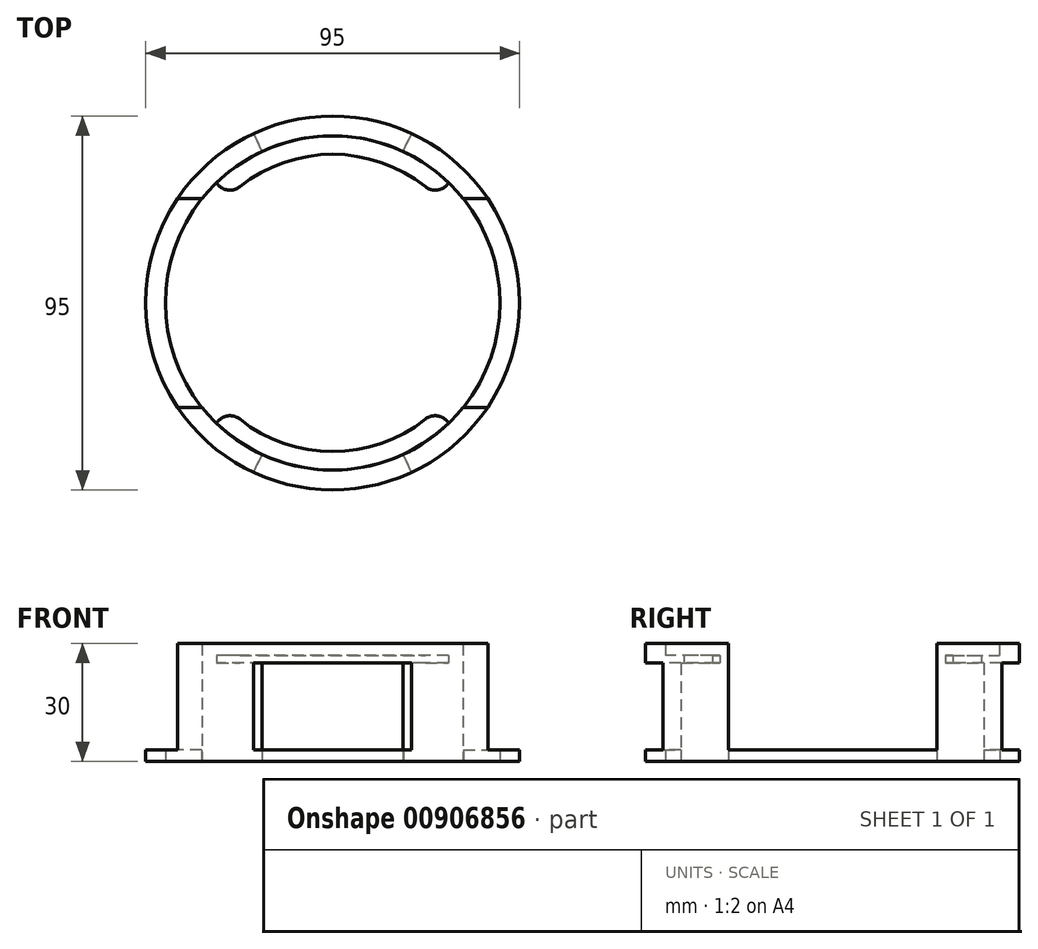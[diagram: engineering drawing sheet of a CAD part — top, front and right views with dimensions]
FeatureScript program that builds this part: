
annotation { "Feature Type Name" : "Feature", "Feature Type Description" : "" }
export const myFeature = defineFeature(function(context is Context, id is Id, definition is map)
    precondition{}
    {
        {
            var Q0;
            Q0=qCreatedBy(makeId("Top.planeOp"),FACE);
            var sketch = newSketch(context, id + "F0", { "sketchPlane" : qUnion([Q0])});
            skCircle(sketch, "E0", {"center": v(0, 0) * mm, "radius": 47.5 * mm});
            skCircle(sketch, "E1", {"center": v(0, 0) * mm, "radius": 42.5 * mm});
            skSolve(sketch);
        }
        {
            var Q0;
            Q0 = qSketchRegion(id + "F0", true);
            extrude(context, id + "F1", {"entities" : qUnion([Q0]), "depth" : 3 * mm, "offsetDistance" : 25 * mm});
        }
        {
            var Q0;
            Q0=qCreatedBy(makeId("Top.planeOp"),FACE);
            var sketch = newSketch(context, id + "F2", { "sketchPlane" : qUnion([Q0])});
            skLineSegment(sketch, "E2", {"start": v(0, 0) * mm, "end": v(-30.48, 65.37) * mm, "construction": true});
            skArc(sketch, "E3", {"start": v(-20.07, 43.05) * mm, "mid": v(-30.88, 36.1) * mm, "end": v(-39.42, 26.5) * mm});
            skLineSegment(sketch, "E4", {"start": v(-20.07, 43.05) * mm, "end": v(-17.94, 38.48) * mm});
            skLineSegment(sketch, "E5", {"start": v(-59.94, 25.5) * mm, "end": v(67.22, 25.5) * mm, "construction": true});
            skLineSegment(sketch, "E6.MirrorCS", {"start": v(-59.94, -25.5) * mm, "end": v(67.22, -25.5) * mm, "construction": true});
            skArc(sketch, "E7", {"start": v(-17.94, 38.48) * mm, "mid": v(-26.25, 33.37) * mm, "end": v(-33.17, 26.5) * mm});
            skLineSegment(sketch, "E8", {"start": v(-39.42, 26.5) * mm, "end": v(-33.17, 26.5) * mm});
            skLineSegment(sketch, "E9", {"start": v(-17.94, 38.48) * mm, "end": v(-20.07, 43.05) * mm});
            skLineSegment(sketch, "E10.MirrorCS", {"start": v(-17.94, -38.48) * mm, "end": v(-20.07, -43.05) * mm});
            skArc(sketch, "E11.MirrorCS", {"start": v(-17.94, -38.48) * mm, "mid": v(-26.25, -33.37) * mm, "end": v(-33.17, -26.5) * mm});
            skArc(sketch, "E12.MirrorCS", {"start": v(-20.07, -43.05) * mm, "mid": v(-30.88, -36.1) * mm, "end": v(-39.42, -26.5) * mm});
            skLineSegment(sketch, "E13.MirrorCS", {"start": v(-20.07, -43.05) * mm, "end": v(-17.94, -38.48) * mm});
            skLineSegment(sketch, "E14.MirrorCS", {"start": v(-39.42, -26.5) * mm, "end": v(-33.17, -26.5) * mm});
            skLineSegment(sketch, "E15.MirrorCS", {"start": v(17.94, 38.48) * mm, "end": v(20.07, 43.05) * mm});
            skLineSegment(sketch, "E16.MirrorCS", {"start": v(17.94, -38.48) * mm, "end": v(20.07, -43.05) * mm});
            skLineSegment(sketch, "E17.MirrorCS", {"start": v(20.07, -43.05) * mm, "end": v(17.94, -38.48) * mm});
            skLineSegment(sketch, "E18.MirrorCS", {"start": v(20.07, 43.05) * mm, "end": v(17.94, 38.48) * mm});
            skLineSegment(sketch, "E19.MirrorCS", {"start": v(39.42, 26.5) * mm, "end": v(33.17, 26.5) * mm});
            skLineSegment(sketch, "E20.MirrorCS", {"start": v(39.42, -26.5) * mm, "end": v(33.17, -26.5) * mm});
            skArc(sketch, "E21.MirrorCS", {"start": v(20.07, 43.05) * mm, "mid": v(30.88, 36.1) * mm, "end": v(39.42, 26.5) * mm});
            skArc(sketch, "E22.MirrorCS", {"start": v(20.07, -43.05) * mm, "mid": v(30.88, -36.1) * mm, "end": v(39.42, -26.5) * mm});
            skArc(sketch, "E23.MirrorCS", {"start": v(17.94, -38.48) * mm, "mid": v(26.25, -33.37) * mm, "end": v(33.17, -26.5) * mm});
            skArc(sketch, "E24.MirrorCS", {"start": v(17.94, 38.48) * mm, "mid": v(26.25, 33.37) * mm, "end": v(33.17, 26.5) * mm});
            skSolve(sketch);
        }
        {
            var Q0;
            Q0 = qSketchRegion(id + "F2", true);
            extrude(context, id + "F3", {"entities" : qUnion([Q0]), "operationType" : NewBodyOperationType.ADD, "depth" : 25 * mm, "offsetDistance" : 25 * mm});
        }
        {
            var Q0;
            Q0=makeQuery(id+"F3.opExtrude","CAP_FACE",FACE,{"disambiguationData":[OSD([sQuery(id+"F2.wireOp",EDGE,"E4"),sQuery(id+"F2.wireOp",EDGE,"E8"),sQuery(id+"F2.wireOp",EDGE,"E3"),sQuery(id+"F2.wireOp",EDGE,"E7")])],"isStart":false});
            var sketch = newSketch(context, id + "F4", { "sketchPlane" : qUnion([Q0])});
            skPoint(sketch, "E25.0", {"position": v(-39.42, 26.5) * mm});
            skPoint(sketch, "E25.1", {"position": v(39.42, 26.5) * mm});
            skPoint(sketch, "E25.2", {"position": v(33.17, 26.5) * mm});
            skPoint(sketch, "E25.3", {"position": v(-33.17, 26.5) * mm});
            skArc(sketch, "E26", {"start": v(-39.42, 26.5) * mm, "mid": v(0, 47.5) * mm, "end": v(39.42, 26.5) * mm});
            skArc(sketch, "E27", {"start": v(-33.17, 26.5) * mm, "mid": v(0, 42.46) * mm, "end": v(33.17, 26.5) * mm});
            skLineSegment(sketch, "E28", {"start": v(-39.42, 26.5) * mm, "end": v(-33.17, 26.5) * mm});
            skLineSegment(sketch, "E29", {"start": v(33.17, 26.5) * mm, "end": v(39.42, 26.5) * mm});
            skLineSegment(sketch, "E30.MirrorCS", {"start": v(-39.42, -26.5) * mm, "end": v(-33.17, -26.5) * mm});
            skLineSegment(sketch, "E31.MirrorCS", {"start": v(33.17, -26.5) * mm, "end": v(39.42, -26.5) * mm});
            skPoint(sketch, "E32.MirrorP", {"position": v(-39.42, -26.5) * mm});
            skPoint(sketch, "E33.MirrorP", {"position": v(39.42, -26.5) * mm});
            skArc(sketch, "E34.MirrorCS", {"start": v(-33.17, -26.5) * mm, "mid": v(0, -42.46) * mm, "end": v(33.17, -26.5) * mm});
            skArc(sketch, "E35.MirrorCS", {"start": v(-39.42, -26.5) * mm, "mid": v(0, -47.5) * mm, "end": v(39.42, -26.5) * mm});
            skPoint(sketch, "E36.MirrorP", {"position": v(33.17, -26.5) * mm});
            skPoint(sketch, "E37.MirrorP", {"position": v(-33.17, -26.5) * mm});
            skSolve(sketch);
        }
        {
            var Q0;
            Q0=qCreatedBy(makeId("Top.planeOp"),FACE);
            cPlane(context, id + "F5", {"entities" : qUnion([Q0]), "cplaneType" : CPlaneType.OFFSET, "offset" : 25 * mm, "width" : 150 * mm, "height" : 150 * mm});
        }
        {
            var Q0;
            Q0=qCreatedBy(id+"F5.planeOp",FACE);
            var sketch = newSketch(context, id + "F6", { "sketchPlane" : qUnion([Q0])});
            skArc(sketch, "E38.0", {"start": v(29.47, -30.62) * mm, "mid": v(0, -42.5) * mm, "end": v(-29.47, -30.62) * mm});
            skLineSegment(sketch, "E39", {"start": v(-29.47, -30.62) * mm, "end": v(-29.47, -23.62) * mm});
            skLineSegment(sketch, "E40", {"start": v(29.47, -30.62) * mm, "end": v(29.47, -23.62) * mm});
            skArc(sketch, "E41", {"start": v(-29.47, -23.62) * mm, "mid": v(0, -37.77) * mm, "end": v(29.47, -23.62) * mm});
            skArc(sketch, "E42.MirrorCS", {"start": v(29.47, 30.62) * mm, "mid": v(0, 42.5) * mm, "end": v(-29.47, 30.62) * mm});
            skLineSegment(sketch, "E43.MirrorCS", {"start": v(29.47, 30.62) * mm, "end": v(29.47, 23.62) * mm});
            skLineSegment(sketch, "E44.MirrorCS", {"start": v(-29.47, 30.62) * mm, "end": v(-29.47, 23.62) * mm});
            skArc(sketch, "E45.MirrorCS", {"start": v(-29.47, 23.62) * mm, "mid": v(0, 37.77) * mm, "end": v(29.47, 23.62) * mm});
            skSolve(sketch);
        }
        {
            var Q0;
            Q0 = qSketchRegion(id + "F4", true);
            extrude(context, id + "F7", {"entities" : qUnion([Q0]), "operationType" : NewBodyOperationType.ADD, "depth" : 5 * mm, "offsetDistance" : 25 * mm});
        }
        {
            var Q0;
            Q0 = qSketchRegion(id + "F6", true);
            extrude(context, id + "F8", {"entities" : qUnion([Q0]), "operationType" : NewBodyOperationType.ADD, "depth" : 2 * mm, "offsetDistance" : 25 * mm});
        }
        {
            var Q0;
            Q0=makeQuery(id+"F8.opExtrude","SWEPT_EDGE",EDGE,{"disambiguationData":[OSD([sQuery(id+"F6.wireOp",EDGE,"E39"),sQuery(id+"F6.wireOp",EDGE,"E41")])]});
            var Q1;
            Q1=makeQuery(id+"F8.opExtrude","SWEPT_EDGE",EDGE,{"disambiguationData":[OSD([sQuery(id+"F6.wireOp",EDGE,"E40"),sQuery(id+"F6.wireOp",EDGE,"E41")])]});
            var Q2;
            Q2=makeQuery(id+"F8.opExtrude","SWEPT_EDGE",EDGE,{"disambiguationData":[OSD([sQuery(id+"F6.wireOp",EDGE,"E43.MirrorCS"),sQuery(id+"F6.wireOp",EDGE,"E45.MirrorCS")])]});
            var Q3;
            Q3=makeQuery(id+"F8.opExtrude","SWEPT_EDGE",EDGE,{"disambiguationData":[OSD([sQuery(id+"F6.wireOp",EDGE,"E44.MirrorCS"),sQuery(id+"F6.wireOp",EDGE,"E45.MirrorCS")])]});
            fillet(context, id + "F9", {"entities" : qUnion([Q0, Q1, Q2, Q3]), "radius" : 4 * mm, "tangentPropagation" : true, "allowEdgeOverflow" : false});
        }
    });
